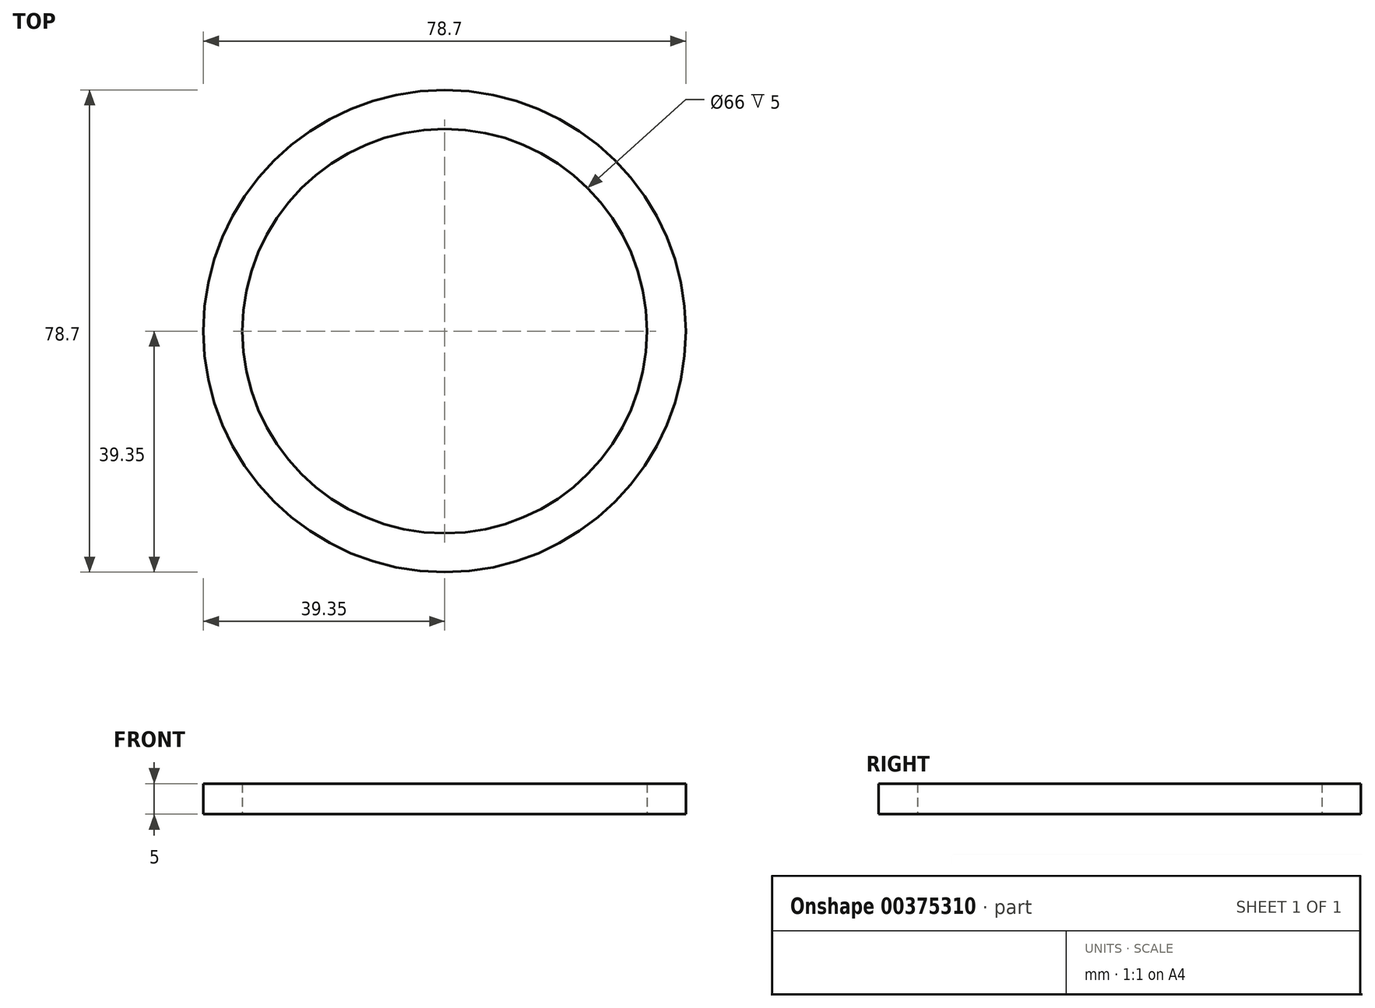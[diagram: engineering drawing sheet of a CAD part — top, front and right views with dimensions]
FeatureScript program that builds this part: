
annotation { "Feature Type Name" : "Feature", "Feature Type Description" : "" }
export const myFeature = defineFeature(function(context is Context, id is Id, definition is map)
    precondition{}
    {
        {
            var Q0;
            Q0=qCreatedBy(makeId("Top.planeOp"),FACE);
            var sketch = newSketch(context, id + "F0", { "sketchPlane" : qUnion([Q0])});
            skCircle(sketch, "E0", {"center": v(0, 0) * mm, "radius": 39.35 * mm});
            skCircle(sketch, "E1", {"center": v(0, 0) * mm, "radius": 33 * mm});
            skSolve(sketch);
        }
        {
            var Q0;
            Q0 = qSketchRegion(id + "F0", true);
            extrude(context, id + "F1", {"entities" : qUnion([Q0]), "depth" : 5 * mm});
        }
    });
